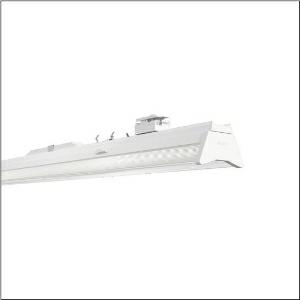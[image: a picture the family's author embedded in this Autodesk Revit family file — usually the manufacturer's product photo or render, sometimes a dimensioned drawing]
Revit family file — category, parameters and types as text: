
# Revit family: licross_r__21_performance_ho_52td16mn4e5m_6ed4
name_source: partatom
category: Lighting Fixtures
units: mm (PartAtom-declared; Revit-internal decimal feet)

## family parameters
Cut with Voids When Loaded = No
Host = Face
Light Source = No
Part Type = Normal
Room Calculation Point = No
Round Connector Dimension = Use Diameter
Shared = No

## types (1)
- --- (1 x LED, 14970 lm, 83.2 W, 4000K)
    Apparent Load = 83 VA
    CIE Flux Codes = 63 87 95 78 100
    Color Rendering = 80
    Color Temperature = 4000K
    Default Elevation = 1800 mm
    Description = Licross® 21 Performance HO, luminaire insert, of sheet steel, galvanised, coil coated, white, length: 1.500mm, width: 120mm, height: 123mm, LED rated luminous flux: 14.970lm, light colour: 840, control gear: ON/OFF Multilumen, with plug, 3-pole, with phase selection, mains connection: 220..240V, AC, 50/60Hz, rated input power: 83W, internal wiring halogen-free, primary light control with lens, of plastic, primary optical cover: cover, of PMMA, light emission: direct/indirect distribution, primary light characteristic: symmetric, protection rating (complete): IP54, insulation class (complete): insulation class I (protective earthing), certification: CE, ENEC, UKCA, protection symbol: D if used in an environment with non-conductive dust loads with corresponding accessories, impact resistance: IK06, permissible ambient temperature for indoor applications: -35..+35°C, corresponds to IFS (International Featured Standards) requirements for safety and quality in the food industry, reducing of maximum allowable ambient temperature of 5°C with ceiling mounting, LABS conformity tested according to VDMA 24364:2018-05, packaging unit: 1 piece
    Height = 114 mm
    Lamp = 1 x LED
    Lamp Light Flux = 14970 lm
    Lamp Power = 83.2 W
    Lamp count = 1
    Length = 1500 mm
    Luminous efficacy = 180 lm/W
    Manufacturer = Siteco
    ModVariant = No
    Model = 52TD16MN4E5M
    Mounting Place = Ceiling
    Mounting Type = Pendant
    Number of Poles = 1
    OnlyDefault = Yes
    Power Factor = 1
    Product Name = Licross® 21 Performance HO
    Product group = luminaire insert | ceiling pendant
    ProductGroupID = 902
    Protection Class = Protection class I
    Protection Degree = IP 54
    RLX_Detail_Level = 1
    RLX_Emergency_Light_Flux = 0 lm
    RLX_Emergency_Type = 0
    RLX_Emergency_Type_DB = No
    RlxData = <blob elided: 31781 chars, md5=8e52ffeb>
    Socket = socket
    Standby Power = 0 W
    System Light Flux = 14970 lm
    System Power = 83 W
    Type Comments = factory setting: luminous flux: 100 % | (A | C | E) | 195 mA
    Type Image = l_1256138.jpg
    URL = http://relux.com
    VarID = @adj_130673
    Voltage = 0 V
    Weight = 0.00 kg
    Width = 120 mm

## geometry (parser evidence)
native form markers: Blend x4, Sweep x13
no freeform markers — native parametric forms only
